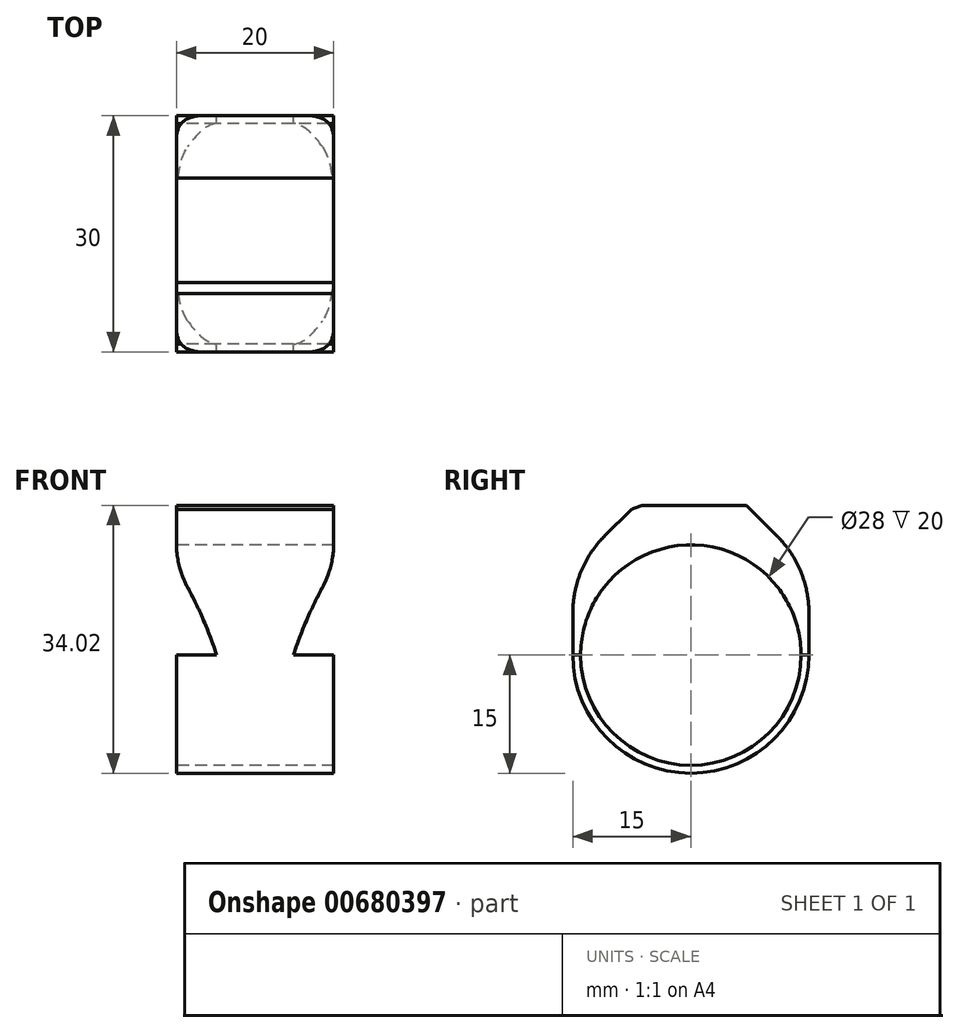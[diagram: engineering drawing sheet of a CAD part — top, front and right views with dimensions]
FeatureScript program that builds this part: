
annotation { "Feature Type Name" : "Feature", "Feature Type Description" : "" }
export const myFeature = defineFeature(function(context is Context, id is Id, definition is map)
    precondition{}
    {
        {
            var Q0;
            Q0=qCreatedBy(makeId("Right.planeOp"),FACE);
            var sketch = newSketch(context, id + "F0", { "sketchPlane" : qUnion([Q0])});
            skCircle(sketch, "E0", {"center": v(0, 0) * mm, "radius": 14 * mm});
            skArc(sketch, "E1", {"start": v(-15, 0) * mm, "mid": v(0, -15) * mm, "end": v(15, 0) * mm});
            skLineSegment(sketch, "E2", {"start": v(15, 0) * mm, "end": v(15, 21.08) * mm});
            skLineSegment(sketch, "E3", {"start": v(-15, 0) * mm, "end": v(-15, 21.08) * mm});
            skLineSegment(sketch, "E4", {"start": v(-15, 21.08) * mm, "end": v(15, 21.08) * mm});
            skSolve(sketch);
        }
        {
            var Q0;
            Q0=qSketchRegion(id+"F0",true);
            extrude(context, id + "F1", {"entities" : qUnion([Q0]), "depth" : 20 * mm, "offsetDistance" : 25 * mm});
        }
        {
            var Q0;
            Q0=makeQuery(id+"F1.opExtrude","SWEPT_EDGE",EDGE,{"disambiguationData":[OSD([sQuery(id+"F0.wireOp",EDGE,"E3"),sQuery(id+"F0.wireOp",EDGE,"E4")])]});
            var Q1;
            Q1=makeQuery(id+"F1.opExtrude","SWEPT_EDGE",EDGE,{"disambiguationData":[OSD([sQuery(id+"F0.wireOp",EDGE,"E2"),sQuery(id+"F0.wireOp",EDGE,"E4")])]});
            chamfer(context, id + "F2", {"entities" : qUnion([Q0, Q1]), "width" : 10 * mm, "tangentPropagation" : true});
        }
        {
            var Q0;
            Q0=makeQuery(id+"F1.opExtrude","SWEPT_FACE",FACE,{"disambiguationData":[OSD([sQuery(id+"F0.wireOp",EDGE,"E2")])]});
            var sketch = newSketch(context, id + "F3", { "sketchPlane" : qUnion([Q0])});
            skLineSegment(sketch, "E5", {"start": v(0, -15) * mm, "end": v(-20, -15) * mm});
            skLineSegment(sketch, "E6", {"start": v(-12.5, -15) * mm, "end": v(-7.5, -15) * mm});
            skArc(sketch, "E7", {"start": v(0, 11.08) * mm, "mid": v(-5.55, -1.44) * mm, "end": v(-7.5, -15) * mm});
            skArc(sketch, "E8", {"start": v(-12.5, -15) * mm, "mid": v(-14.45, -1.44) * mm, "end": v(-20, 11.08) * mm});
            skLineSegment(sketch, "E9", {"start": v(0, 11.08) * mm, "end": v(0, -15) * mm});
            skLineSegment(sketch, "E10", {"start": v(0, -15) * mm, "end": v(-7.5, -15) * mm});
            skLineSegment(sketch, "E11", {"start": v(-20, -15) * mm, "end": v(-20, -15) * mm});
            skLineSegment(sketch, "E12", {"start": v(-20, 11.08) * mm, "end": v(-20, -15) * mm});
            skLineSegment(sketch, "E13.trimOffspring", {"start": v(-12.5, -15) * mm, "end": v(-20, -15) * mm});
            skSolve(sketch);
        }
        {
            var Q0;
            {var subQ0=sQuery(id+"F3.wireOp",EDGE,"E9");var subQ2=sQuery(id+"F0.wireOp",EDGE,"E2");var subQ4=makeQuery(id+"F1.opExtrude","SWEPT_EDGE",EDGE,{"disambiguationData":[OSD([sQuery(id+"F0.wireOp",EDGE,"E1"),subQ2])]});var subQ6=makeQuery(id+"F3.imprint","INTERSECT",VERTEX,{"derivedFrom":[subQ4,subQ0]});Q0=makeQuery(id+"F3.imprint","IMPRINT",FACE,{"disambiguationData":[TD([[makeQuery(id+"F3.imprint","IMPRINT",EDGE,{"disambiguationData":[TD([[subQ6,1.0]])],"derivedFrom":subQ4}),1.0]])]});}
            var Q1;
            {var subQ0=sQuery(id+"F3.wireOp",EDGE,"E12");var subQ2=sQuery(id+"F0.wireOp",EDGE,"E2");var subQ4=makeQuery(id+"F1.opExtrude","SWEPT_EDGE",EDGE,{"disambiguationData":[OSD([sQuery(id+"F0.wireOp",EDGE,"E1"),subQ2])]});var subQ6=makeQuery(id+"F3.imprint","INTERSECT",VERTEX,{"derivedFrom":[subQ4,subQ0]});Q1=makeQuery(id+"F3.imprint","IMPRINT",FACE,{"disambiguationData":[TD([[makeQuery(id+"F3.imprint","IMPRINT",EDGE,{"disambiguationData":[TD([[subQ6,-1.0]])],"derivedFrom":subQ4}),1.0]])]});}
            var Q2;
            {var subQ0=sQuery(id+"F3.wireOp",EDGE,"E13.trimOffspring");Q2=makeQuery(id+"F3.imprint","IMPRINT",FACE,{"disambiguationData":[TD([[makeQuery(id+"F3.imprint","IMPRINT",EDGE,{"derivedFrom":subQ0}),-1.0]])]});}
            var Q3;
            {var subQ0=sQuery(id+"F3.wireOp",EDGE,"E10");Q3=makeQuery(id+"F3.imprint","IMPRINT",FACE,{"disambiguationData":[TD([[makeQuery(id+"F3.imprint","IMPRINT",EDGE,{"derivedFrom":subQ0}),-1.0]])]});}
            extrude(context, id + "F4", {"entities" : qUnion([Q0, Q1, Q2, Q3]), "operationType" : NewBodyOperationType.REMOVE, "oppositeDirection" : true, "depth" : 38.66 * mm, "offsetDistance" : 25 * mm});
        }
        {
            var Q0;
            {var subQ0=sQuery(id+"F0.wireOp",EDGE,"E2");Q0=makeQuery(id+"F2.opChamfer","BLEND_EDGE",EDGE,{"blendedFrom":[makeQuery(id+"F1.opExtrude","SWEPT_EDGE",EDGE,{"disambiguationData":[OSD([subQ0,sQuery(id+"F0.wireOp",EDGE,"E4")])]}),makeQuery(id+"F1.opExtrude","SWEPT_FACE",FACE,{"disambiguationData":[OSD([subQ0])]})],"blendedInto":[makeQuery(id+"F1.opExtrude","SWEPT_FACE",FACE,{"disambiguationData":[OSD([subQ0])]})]});}
            var Q1;
            {var subQ0=sQuery(id+"F0.wireOp",EDGE,"E3");Q1=makeQuery(id+"F2.opChamfer","BLEND_EDGE",EDGE,{"blendedFrom":[makeQuery(id+"F1.opExtrude","SWEPT_EDGE",EDGE,{"disambiguationData":[OSD([subQ0,sQuery(id+"F0.wireOp",EDGE,"E4")])]}),makeQuery(id+"F1.opExtrude","SWEPT_FACE",FACE,{"disambiguationData":[OSD([subQ0])]})],"blendedInto":[makeQuery(id+"F1.opExtrude","SWEPT_FACE",FACE,{"disambiguationData":[OSD([subQ0])]})]});}
            fillet(context, id + "F5", {"entities" : qUnion([Q0, Q1]), "radius" : 13.84 * mm, "tangentPropagation" : true, "allowEdgeOverflow" : false});
        }
        {
            var Q0;
            {var subQ0=sQuery(id+"F0.wireOp",EDGE,"E4");var subQ1=sQuery(id+"F0.wireOp",EDGE,"E2");var subQ3=sQuery(id+"F3.wireOp",EDGE,"E8");Q0=makeQuery(id+"F4.boolean.opBoolean","COPY",EDGE,{"disambiguationData":[TD([makeQuery(id+"F1.opExtrude","SWEPT_FACE",FACE,{"disambiguationData":[OSD([subQ1])]})])],"derivedFrom":makeQuery(id+"F4.opExtrude","SWEPT_EDGE",EDGE,{"disambiguationData":[OSD([subQ1,subQ0,subQ3,sQuery(id+"F3.wireOp",EDGE,"E12")])]})});}
            var Q1;
            {var subQ0=sQuery(id+"F0.wireOp",EDGE,"E4");var subQ1=sQuery(id+"F0.wireOp",EDGE,"E3");var subQ2=sQuery(id+"F0.wireOp",EDGE,"E2");var subQ4=sQuery(id+"F3.wireOp",EDGE,"E8");Q1=makeQuery(id+"F4.boolean.opBoolean","COPY",EDGE,{"disambiguationData":[TD([makeQuery(id+"F1.opExtrude","SWEPT_FACE",FACE,{"disambiguationData":[OSD([subQ1])]})])],"derivedFrom":makeQuery(id+"F4.opExtrude","SWEPT_EDGE",EDGE,{"disambiguationData":[OSD([subQ2,subQ0,subQ4,sQuery(id+"F3.wireOp",EDGE,"E12")])]})});}
            var Q2;
            {var subQ0=sQuery(id+"F0.wireOp",EDGE,"E4");var subQ1=sQuery(id+"F0.wireOp",EDGE,"E3");var subQ2=sQuery(id+"F3.wireOp",EDGE,"E7");var subQ3=sQuery(id+"F0.wireOp",EDGE,"E2");Q2=makeQuery(id+"F4.boolean.opBoolean","COPY",EDGE,{"disambiguationData":[TD([makeQuery(id+"F1.opExtrude","SWEPT_FACE",FACE,{"disambiguationData":[OSD([subQ1])]})])],"derivedFrom":makeQuery(id+"F4.opExtrude","SWEPT_EDGE",EDGE,{"disambiguationData":[OSD([subQ3,subQ0,subQ2,sQuery(id+"F3.wireOp",EDGE,"E9")])]})});}
            var Q3;
            {var subQ0=sQuery(id+"F0.wireOp",EDGE,"E2");var subQ1=sQuery(id+"F0.wireOp",EDGE,"E4");var subQ3=sQuery(id+"F3.wireOp",EDGE,"E7");Q3=makeQuery(id+"F4.boolean.opBoolean","COPY",EDGE,{"disambiguationData":[TD([makeQuery(id+"F1.opExtrude","SWEPT_FACE",FACE,{"disambiguationData":[OSD([subQ0])]})])],"derivedFrom":makeQuery(id+"F4.opExtrude","SWEPT_EDGE",EDGE,{"disambiguationData":[OSD([subQ0,subQ1,subQ3,sQuery(id+"F3.wireOp",EDGE,"E9")])]})});}
            fillet(context, id + "F6", {"entities" : qUnion([Q0, Q1, Q2, Q3]), "radius" : 12 * mm, "tangentPropagation" : true, "allowEdgeOverflow" : false});
        }
        {
            var Q0;
            Q0=qCreatedBy(makeId("Right.planeOp"),FACE);
            var sketch = newSketch(context, id + "F7", { "sketchPlane" : qUnion([Q0])});
            skLineSegment(sketch, "E14.bottom", {"start": v(23.02, 60.04) * mm, "end": v(-26.86, 60.04) * mm});
            skLineSegment(sketch, "E14.top", {"start": v(23.02, 19.02) * mm, "end": v(-26.86, 19.02) * mm});
            skLineSegment(sketch, "E14.left", {"start": v(23.02, 60.04) * mm, "end": v(23.02, 19.02) * mm});
            skLineSegment(sketch, "E14.right", {"start": v(-26.86, 60.04) * mm, "end": v(-26.86, 19.02) * mm});
            skSolve(sketch);
        }
        {
            var Q0;
            Q0=qSketchRegion(id+"F7",true);
            extrude(context, id + "F8", {"entities" : qUnion([Q0]), "operationType" : NewBodyOperationType.REMOVE, "endBound" : BoundingType.SYMMETRIC, "oppositeDirection" : true, "depth" : 77.2 * mm, "offsetDistance" : 25 * mm});
        }
        {
            var Q0;
            Q0=qCreatedBy(makeId("Right.planeOp"),FACE);
            var sketch = newSketch(context, id + "F9", { "sketchPlane" : qUnion([Q0])});
            skCircle(sketch, "E15", {"center": v(0, 0) * mm, "radius": 20 * mm});
            skCircle(sketch, "E16", {"center": v(0, 20) * mm, "radius": 2.5 * mm});
            skCircle(sketch, "E17.1.1", {"center": v(-3.57, 19.68) * mm, "radius": 2.5 * mm});
            skCircle(sketch, "E17.2.1", {"center": v(-7.03, 18.72) * mm, "radius": 2.5 * mm});
            skCircle(sketch, "E18.2.3.0", {"center": v(-10.26, 17.17) * mm, "radius": 2.5 * mm});
            skCircle(sketch, "E19.2.4.0", {"center": v(-13.16, 15.06) * mm, "radius": 2.5 * mm});
            skCircle(sketch, "E19.2.5.0", {"center": v(-15.64, 12.47) * mm, "radius": 2.5 * mm});
            skCircle(sketch, "E19.2.6.0", {"center": v(-17.61, 9.48) * mm, "radius": 2.5 * mm});
            skCircle(sketch, "E19.2.7.0", {"center": v(-19.02, 6.18) * mm, "radius": 2.5 * mm});
            skCircle(sketch, "E19.2.8.0", {"center": v(-19.82, 2.68) * mm, "radius": 2.5 * mm});
            skCircle(sketch, "E19.2.9.0", {"center": v(-19.98, -0.9) * mm, "radius": 2.5 * mm});
            skCircle(sketch, "E19.2.10.0", {"center": v(-19.5, -4.45) * mm, "radius": 2.5 * mm});
            skCircle(sketch, "E19.2.11.0", {"center": v(-18.4, -7.86) * mm, "radius": 2.5 * mm});
            skCircle(sketch, "E19.2.12.0", {"center": v(-16.7, -11.02) * mm, "radius": 2.5 * mm});
            skCircle(sketch, "E19.2.13.0", {"center": v(-14.46, -13.82) * mm, "radius": 2.5 * mm});
            skCircle(sketch, "E19.2.14.0", {"center": v(-11.76, -16.18) * mm, "radius": 2.5 * mm});
            skCircle(sketch, "E19.2.15.0", {"center": v(-8.68, -18.02) * mm, "radius": 2.5 * mm});
            skCircle(sketch, "E19.2.16.0", {"center": v(-5.32, -19.28) * mm, "radius": 2.5 * mm});
            skCircle(sketch, "E19.2.17.0", {"center": v(-1.8, -19.92) * mm, "radius": 2.5 * mm});
            skCircle(sketch, "E19.2.18.0", {"center": v(1.8, -19.92) * mm, "radius": 2.5 * mm});
            skCircle(sketch, "E19.2.19.0", {"center": v(5.32, -19.28) * mm, "radius": 2.5 * mm});
            skCircle(sketch, "E20.2.20.0", {"center": v(8.68, -18.02) * mm, "radius": 2.5 * mm});
            skCircle(sketch, "E20.2.21.0", {"center": v(11.76, -16.18) * mm, "radius": 2.5 * mm});
            skCircle(sketch, "E20.2.22.0", {"center": v(14.46, -13.82) * mm, "radius": 2.5 * mm});
            skCircle(sketch, "E20.2.23.0", {"center": v(16.7, -11.02) * mm, "radius": 2.5 * mm});
            skCircle(sketch, "E20.2.24.0", {"center": v(18.4, -7.86) * mm, "radius": 2.5 * mm});
            skCircle(sketch, "E20.2.25.0", {"center": v(19.5, -4.45) * mm, "radius": 2.5 * mm});
            skCircle(sketch, "E20.2.26.0", {"center": v(19.98, -0.9) * mm, "radius": 2.5 * mm});
            skCircle(sketch, "E20.2.27.0", {"center": v(19.82, 2.68) * mm, "radius": 2.5 * mm});
            skCircle(sketch, "E20.2.28.0", {"center": v(19.02, 6.18) * mm, "radius": 2.5 * mm});
            skCircle(sketch, "E20.2.29.0", {"center": v(17.61, 9.48) * mm, "radius": 2.5 * mm});
            skCircle(sketch, "E21.2.30.0", {"center": v(15.64, 12.47) * mm, "radius": 2.5 * mm});
            skCircle(sketch, "E21.2.31.0", {"center": v(13.16, 15.06) * mm, "radius": 2.5 * mm});
            skCircle(sketch, "E21.2.32.0", {"center": v(10.26, 17.17) * mm, "radius": 2.5 * mm});
            skCircle(sketch, "E21.2.33.0", {"center": v(7.03, 18.72) * mm, "radius": 2.5 * mm});
            skCircle(sketch, "E21.2.34.0", {"center": v(3.57, 19.68) * mm, "radius": 2.5 * mm});
            skSolve(sketch);
        }
        {
            var Q0;
            {var subQ0=sQuery(id+"F9.wireOp",EDGE,"E15");var subQ1=sQuery(id+"F9.wireOp",EDGE,"E20.2.29.0");var subQ2=makeQuery(id+"F9.imprint","INTERSECT",VERTEX,{"disambiguationData":[OD(0.0)],"derivedFrom":[subQ1,subQ0]});Q0=makeQuery(id+"F9.imprint","IMPRINT",FACE,{"disambiguationData":[TD([[makeQuery(id+"F9.imprint","IMPRINT",EDGE,{"disambiguationData":[TD([[subQ2,-1.0]])],"derivedFrom":subQ1}),-1.0]])]});}
            var Q1;
            {var subQ0=sQuery(id+"F9.wireOp",EDGE,"E15");var subQ1=sQuery(id+"F9.wireOp",EDGE,"E21.2.30.0");var subQ2=makeQuery(id+"F9.imprint","INTERSECT",VERTEX,{"disambiguationData":[OD(0.0)],"derivedFrom":[subQ1,subQ0]});Q1=makeQuery(id+"F9.imprint","IMPRINT",FACE,{"disambiguationData":[TD([[makeQuery(id+"F9.imprint","IMPRINT",EDGE,{"disambiguationData":[TD([[subQ2,-1.0]])],"derivedFrom":subQ1}),-1.0]])]});}
            var Q2;
            {var subQ0=sQuery(id+"F9.wireOp",EDGE,"E15");var subQ1=sQuery(id+"F9.wireOp",EDGE,"E21.2.31.0");var subQ2=makeQuery(id+"F9.imprint","INTERSECT",VERTEX,{"disambiguationData":[OD(0.0)],"derivedFrom":[subQ1,subQ0]});Q2=makeQuery(id+"F9.imprint","IMPRINT",FACE,{"disambiguationData":[TD([[makeQuery(id+"F9.imprint","IMPRINT",EDGE,{"disambiguationData":[TD([[subQ2,-1.0]])],"derivedFrom":subQ1}),1.0]])]});}
            var Q3;
            {var subQ0=sQuery(id+"F9.wireOp",EDGE,"E15");var subQ1=sQuery(id+"F9.wireOp",EDGE,"E21.2.31.0");var subQ2=makeQuery(id+"F9.imprint","INTERSECT",VERTEX,{"disambiguationData":[OD(0.0)],"derivedFrom":[subQ1,subQ0]});Q3=makeQuery(id+"F9.imprint","IMPRINT",FACE,{"disambiguationData":[TD([[makeQuery(id+"F9.imprint","IMPRINT",EDGE,{"disambiguationData":[TD([[subQ2,-1.0]])],"derivedFrom":subQ1}),-1.0]])]});}
            var Q4;
            {var subQ0=sQuery(id+"F9.wireOp",EDGE,"E15");var subQ1=sQuery(id+"F9.wireOp",EDGE,"E21.2.32.0");var subQ2=makeQuery(id+"F9.imprint","INTERSECT",VERTEX,{"disambiguationData":[OD(0.0)],"derivedFrom":[subQ1,subQ0]});Q4=makeQuery(id+"F9.imprint","IMPRINT",FACE,{"disambiguationData":[TD([[makeQuery(id+"F9.imprint","IMPRINT",EDGE,{"disambiguationData":[TD([[subQ2,-1.0]])],"derivedFrom":subQ1}),1.0]])]});}
            var Q5;
            {var subQ0=sQuery(id+"F9.wireOp",EDGE,"E15");var subQ1=sQuery(id+"F9.wireOp",EDGE,"E17.2.1");var subQ2=makeQuery(id+"F9.imprint","INTERSECT",VERTEX,{"disambiguationData":[OD(0.0)],"derivedFrom":[subQ1,subQ0]});Q5=makeQuery(id+"F9.imprint","IMPRINT",FACE,{"disambiguationData":[TD([[makeQuery(id+"F9.imprint","IMPRINT",EDGE,{"disambiguationData":[TD([[subQ2,-1.0]])],"derivedFrom":subQ1}),1.0]])]});}
            var Q6;
            {var subQ0=sQuery(id+"F9.wireOp",EDGE,"E15");var subQ1=sQuery(id+"F9.wireOp",EDGE,"E17.2.1");var subQ2=makeQuery(id+"F9.imprint","INTERSECT",VERTEX,{"disambiguationData":[OD(0.0)],"derivedFrom":[subQ1,subQ0]});Q6=makeQuery(id+"F9.imprint","IMPRINT",FACE,{"disambiguationData":[TD([[makeQuery(id+"F9.imprint","IMPRINT",EDGE,{"disambiguationData":[TD([[subQ2,-1.0]])],"derivedFrom":subQ1}),-1.0]])]});}
            var Q7;
            {var subQ0=sQuery(id+"F9.wireOp",EDGE,"E15");var subQ1=sQuery(id+"F9.wireOp",EDGE,"E18.2.3.0");var subQ2=makeQuery(id+"F9.imprint","INTERSECT",VERTEX,{"disambiguationData":[OD(0.0)],"derivedFrom":[subQ1,subQ0]});Q7=makeQuery(id+"F9.imprint","IMPRINT",FACE,{"disambiguationData":[TD([[makeQuery(id+"F9.imprint","IMPRINT",EDGE,{"disambiguationData":[TD([[subQ2,-1.0]])],"derivedFrom":subQ1}),1.0]])]});}
            var Q8;
            {var subQ0=sQuery(id+"F9.wireOp",EDGE,"E15");var subQ1=sQuery(id+"F9.wireOp",EDGE,"E18.2.3.0");var subQ2=makeQuery(id+"F9.imprint","INTERSECT",VERTEX,{"disambiguationData":[OD(0.0)],"derivedFrom":[subQ1,subQ0]});Q8=makeQuery(id+"F9.imprint","IMPRINT",FACE,{"disambiguationData":[TD([[makeQuery(id+"F9.imprint","IMPRINT",EDGE,{"disambiguationData":[TD([[subQ2,-1.0]])],"derivedFrom":subQ1}),-1.0]])]});}
            var Q9;
            {var subQ0=sQuery(id+"F9.wireOp",EDGE,"E15");var subQ1=sQuery(id+"F9.wireOp",EDGE,"E19.2.4.0");var subQ2=makeQuery(id+"F9.imprint","INTERSECT",VERTEX,{"disambiguationData":[OD(0.0)],"derivedFrom":[subQ1,subQ0]});Q9=makeQuery(id+"F9.imprint","IMPRINT",FACE,{"disambiguationData":[TD([[makeQuery(id+"F9.imprint","IMPRINT",EDGE,{"disambiguationData":[TD([[subQ2,-1.0]])],"derivedFrom":subQ1}),-1.0]])]});}
            extrude(context, id + "F10", {"entities" : qUnion([Q0, Q1, Q2, Q3, Q4, Q5, Q6, Q7, Q8, Q9]), "operationType" : NewBodyOperationType.REMOVE, "depth" : 25 * mm, "offsetDistance" : 25 * mm});
        }
    });
